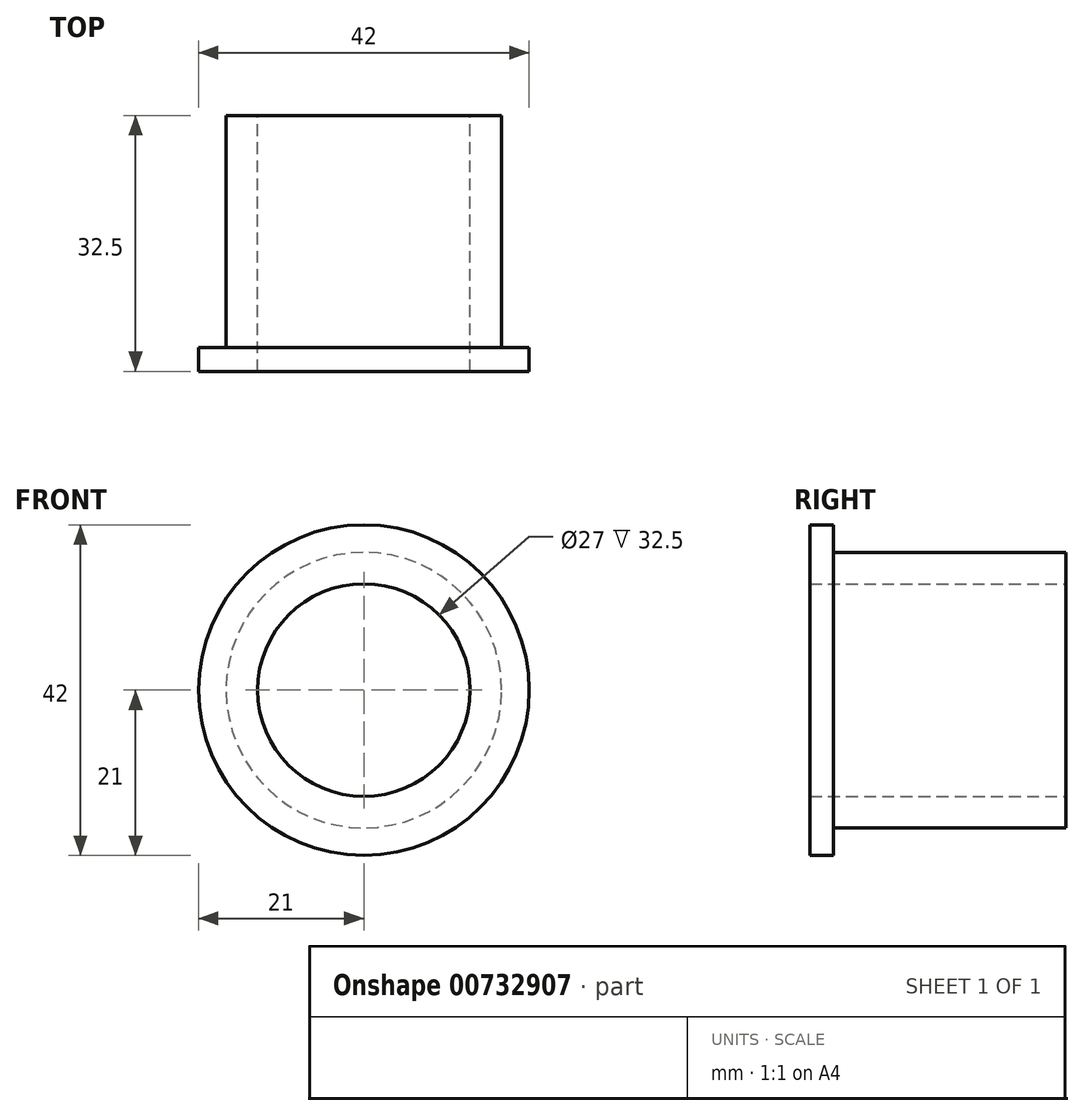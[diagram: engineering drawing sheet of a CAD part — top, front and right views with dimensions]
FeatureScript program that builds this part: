
annotation { "Feature Type Name" : "Feature", "Feature Type Description" : "" }
export const myFeature = defineFeature(function(context is Context, id is Id, definition is map)
    precondition{}
    {
        {
            var Q0;
            Q0=qCreatedBy(makeId("Front.planeOp"),FACE);
            var sketch = newSketch(context, id + "F0", { "sketchPlane" : qUnion([Q0])});
            skCircle(sketch, "E0", {"center": v(0, 0) * mm, "radius": 17.5 * mm});
            skCircle(sketch, "E1", {"center": v(0, 0) * mm, "radius": 21 * mm});
            skCircle(sketch, "E2", {"center": v(0, 0) * mm, "radius": 13.5 * mm});
            skSolve(sketch);
        }
        {
            var Q0;
            Q0 = qSketchRegion(id + "F0", true);
            var Q1;
            Q1=makeQuery(id+"F0.imprint","IMPRINT",FACE,{"disambiguationData":[TD([[makeQuery(id+"F0.imprint","IMPRINT",EDGE,{"derivedFrom":sQuery(id+"F0.wireOp",EDGE,"E0")}),1.0]])]});
            extrude(context, id + "F1", {"entities" : qUnion([Q0, Q1]), "depth" : 3 * mm, "offsetDistance" : 25 * mm});
        }
        {
            var Q0;
            Q0=makeQuery(id+"F1.opExtrude","CAP_FACE",FACE,{"disambiguationData":[OSD([sQuery(id+"F0.wireOp",EDGE,"E1"),sQuery(id+"F0.wireOp",EDGE,"E2")])],"isStart":true});
            var sketch = newSketch(context, id + "F2", { "sketchPlane" : qUnion([Q0])});
            skCircle(sketch, "E3", {"center": v(0, 0) * mm, "radius": 17.5 * mm});
            skSolve(sketch);
        }
        {
            var Q0;
            Q0=makeQuery(id+"F2.imprint","IMPRINT",FACE,{"disambiguationData":[TD([[makeQuery(id+"F2.imprint","IMPRINT",EDGE,{"derivedFrom":sQuery(id+"F2.wireOp",EDGE,"E3")}),1.0]])]});
            extrude(context, id + "F3", {"entities" : qUnion([Q0]), "operationType" : NewBodyOperationType.ADD, "depth" : 29.5 * mm, "offsetDistance" : 25 * mm});
        }
    });
